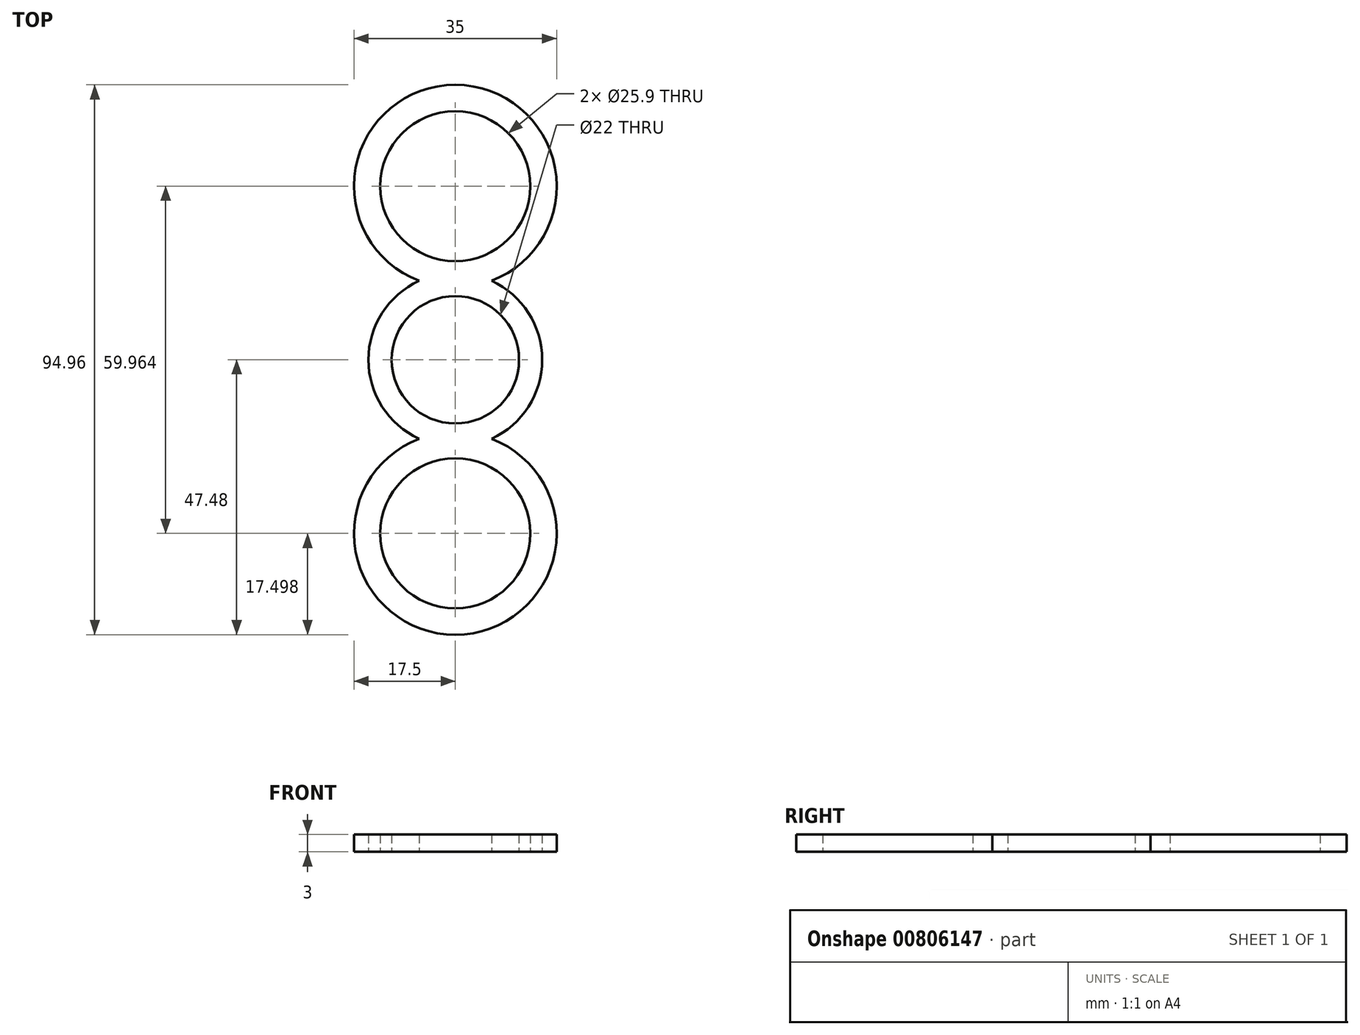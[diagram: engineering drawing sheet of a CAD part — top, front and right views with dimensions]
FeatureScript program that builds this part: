
annotation { "Feature Type Name" : "Feature", "Feature Type Description" : "" }
export const myFeature = defineFeature(function(context is Context, id is Id, definition is map)
    precondition{}
    {
        {
            var Q0;
            Q0=qCreatedBy(makeId("Top.planeOp"),FACE);
            var sketch = newSketch(context, id + "F0", { "sketchPlane" : qUnion([Q0])});
            skCircle(sketch, "E0", {"center": v(0, 0) * mm, "radius": 11 * mm});
            skArc(sketch, "E1", {"start": v(-6.25, 13.64) * mm, "mid": v(-15, 0) * mm, "end": v(-6.25, -13.64) * mm});
            skCircle(sketch, "E2", {"center": v(0, 29.98) * mm, "radius": 12.95 * mm});
            skArc(sketch, "E3", {"start": v(6.25, 13.64) * mm, "mid": v(0, 47.48) * mm, "end": v(-6.25, 13.64) * mm});
            skCircle(sketch, "E4.1.0", {"center": v(0, -29.98) * mm, "radius": 12.95 * mm});
            skArc(sketch, "E4.1.1", {"start": v(-6.25, -13.64) * mm, "mid": v(0, -47.48) * mm, "end": v(6.25, -13.64) * mm});
            skArc(sketch, "E5.trimOffspring", {"start": v(6.25, -13.64) * mm, "mid": v(15, 0) * mm, "end": v(6.25, 13.64) * mm});
            skSolve(sketch);
        }
        {
            var Q0;
            Q0=makeQuery(id+"F0.imprint","IMPRINT",FACE,{"disambiguationData":[TD([[makeQuery(id+"F0.imprint","IMPRINT",EDGE,{"derivedFrom":sQuery(id+"F0.wireOp",EDGE,"E2")}),-1.0]])]});
            extrude(context, id + "F1", {"entities" : qUnion([Q0]), "depth" : 3 * mm, "offsetDistance" : 25 * mm});
        }
    });
